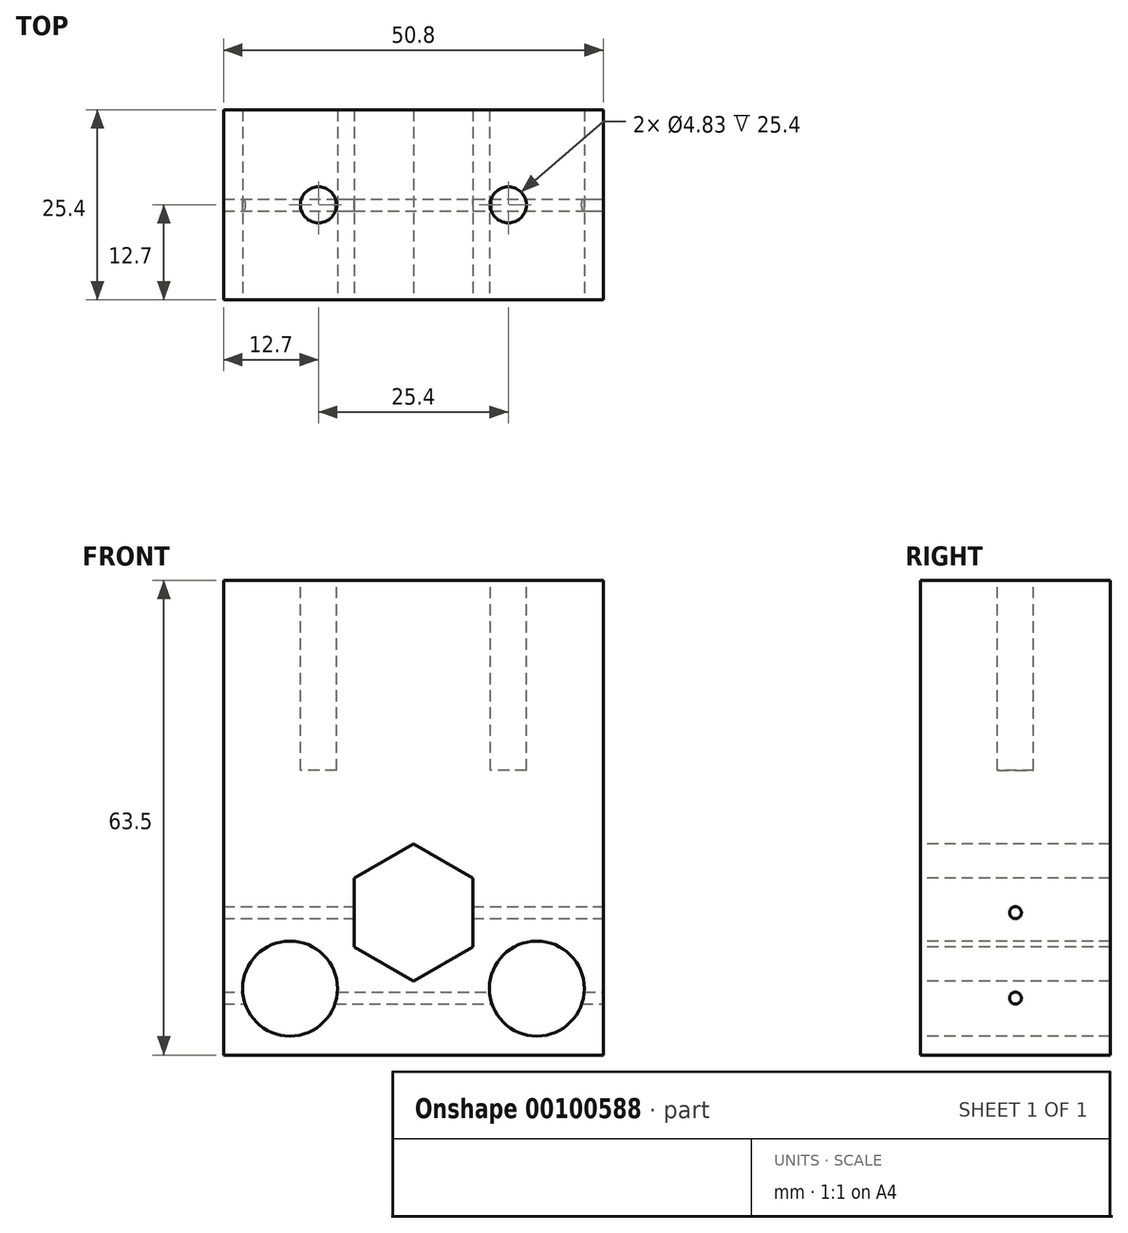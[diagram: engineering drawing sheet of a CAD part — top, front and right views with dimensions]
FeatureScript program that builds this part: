
annotation { "Feature Type Name" : "Feature", "Feature Type Description" : "" }
export const myFeature = defineFeature(function(context is Context, id is Id, definition is map)
    precondition{}
    {
        {
            var Q0;
            Q0=qCreatedBy(makeId("Front.planeOp"),FACE);
            var sketch = newSketch(context, id + "F0", { "sketchPlane" : qUnion([Q0])});
            skLineSegment(sketch, "E0.bottom", {"start": v(-25.4, 44.45) * mm, "end": v(25.4, 44.45) * mm});
            skLineSegment(sketch, "E0.top", {"start": v(-25.4, -19.05) * mm, "end": v(25.4, -19.05) * mm});
            skLineSegment(sketch, "E0.left", {"start": v(-25.4, 44.45) * mm, "end": v(-25.4, -19.05) * mm});
            skLineSegment(sketch, "E0.right", {"start": v(25.4, 44.45) * mm, "end": v(25.4, -19.05) * mm});
            skPoint(sketch, "E1", {"position": v(0, 44.45) * mm});
            skPoint(sketch, "E2", {"position": v(25.4, 12.7) * mm});
            skCircle(sketch, "E3", {"center": v(-16.51, -10.16) * mm, "radius": 6.35 * mm});
            skLineSegment(sketch, "E4", {"start": v(0, 44.45) * mm, "end": v(0, -19.05) * mm, "construction": true});
            skCircle(sketch, "E5.MirrorC", {"center": v(16.51, -10.16) * mm, "radius": 6.35 * mm});
            skCircle(sketch, "E6.cCircle", {"center": v(0, 0) * mm, "radius": 7.94 * mm, "construction": true});
            skLineSegment(sketch, "E6.0", {"start": v(-7.94, -4.58) * mm, "end": v(-7.94, 4.58) * mm});
            skLineSegment(sketch, "E6.1", {"start": v(-7.94, 4.58) * mm, "end": v(0, 9.17) * mm});
            skLineSegment(sketch, "E6.2", {"start": v(0, 9.17) * mm, "end": v(7.94, 4.58) * mm});
            skLineSegment(sketch, "E6.3", {"start": v(7.94, 4.58) * mm, "end": v(7.94, -4.58) * mm});
            skLineSegment(sketch, "E6.4", {"start": v(7.94, -4.58) * mm, "end": v(0, -9.17) * mm});
            skLineSegment(sketch, "E6.5", {"start": v(0, -9.17) * mm, "end": v(-7.94, -4.58) * mm});
            skPoint(sketch, "E6.0.midPoint", {"position": v(-7.94, 0) * mm});
            skSolve(sketch);
        }
        {
            var Q0;
            Q0=makeQuery(id+"F0.imprint","IMPRINT",FACE,{"disambiguationData":[TD([[makeQuery(id+"F0.imprint","IMPRINT",EDGE,{"derivedFrom":sQuery(id+"F0.wireOp",EDGE,"E0.bottom")}),-1.0]])]});
            extrude(context, id + "F1", {"entities" : qUnion([Q0]), "oppositeDirection" : true, "depth" : 25.4 * mm});
        }
        {
            var Q0;
            Q0=makeQuery(id+"F1.opExtrude","SWEPT_FACE",FACE,{"disambiguationData":[OSD([sQuery(id+"F0.wireOp",EDGE,"E0.right")])]});
            var sketch = newSketch(context, id + "F2", { "sketchPlane" : qUnion([Q0])});
            skCircle(sketch, "E7", {"center": v(12.7, -11.43) * mm, "radius": 0.8 * mm});
            skCircle(sketch, "E8", {"center": v(12.7, 0) * mm, "radius": 0.8 * mm});
            skSolve(sketch);
        }
        {
            var Q0;
            Q0 = qSketchRegion(id + "F2", true);
            extrude(context, id + "F3", {"entities" : qUnion([Q0]), "operationType" : NewBodyOperationType.REMOVE, "endBound" : BoundingType.THROUGH_ALL, "oppositeDirection" : true, "depth" : 25.4 * mm});
        }
        {
            var Q0;
            Q0=makeQuery(id+"F1.opExtrude","SWEPT_FACE",FACE,{"disambiguationData":[OSD([sQuery(id+"F0.wireOp",EDGE,"E0.bottom")])]});
            var sketch = newSketch(context, id + "F4", { "sketchPlane" : qUnion([Q0])});
            skCircle(sketch, "E9", {"center": v(12.7, 12.7) * mm, "radius": 2.41 * mm});
            skPoint(sketch, "E9.centerSnap0", {"position": v(25.4, 12.7) * mm});
            skLineSegment(sketch, "E10", {"start": v(0, 25.4) * mm, "end": v(0, 0) * mm, "construction": true});
            skCircle(sketch, "E11.MirrorC", {"center": v(-12.7, 12.7) * mm, "radius": 2.41 * mm});
            skSolve(sketch);
        }
        {
            var Q0;
            Q0 = qSketchRegion(id + "F4", true);
            extrude(context, id + "F5", {"entities" : qUnion([Q0]), "operationType" : NewBodyOperationType.REMOVE, "oppositeDirection" : true, "depth" : 25.4 * mm});
        }
    });
